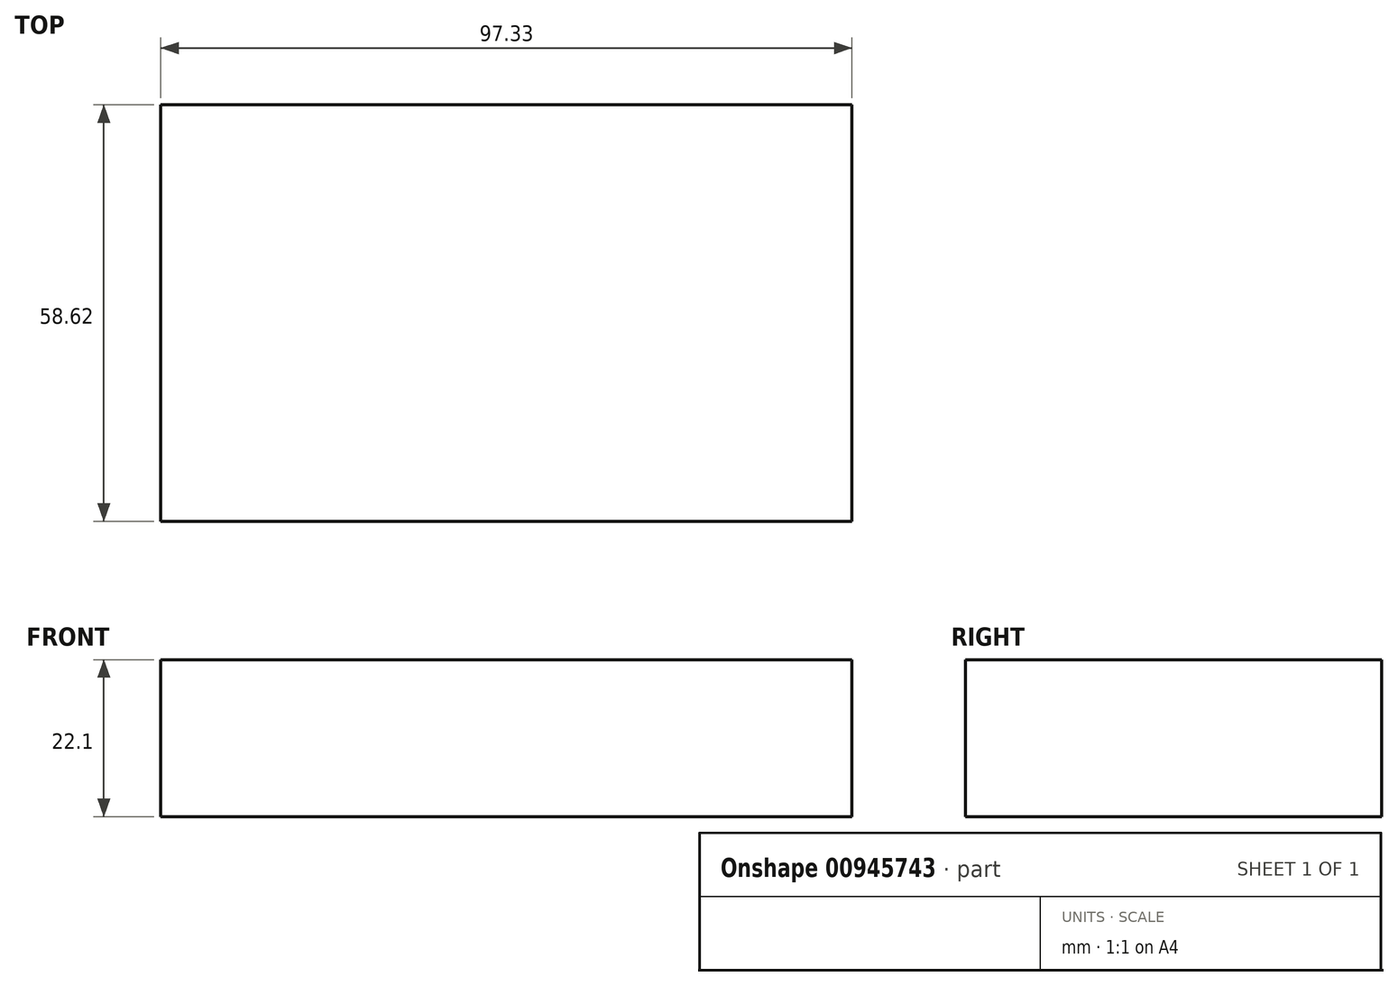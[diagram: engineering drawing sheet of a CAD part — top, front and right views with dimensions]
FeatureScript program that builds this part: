
annotation { "Feature Type Name" : "Feature", "Feature Type Description" : "" }
export const myFeature = defineFeature(function(context is Context, id is Id, definition is map)
    precondition{}
    {
        {
            var Q0;
            Q0=qCreatedBy(makeId("Top.planeOp"),FACE);
            var sketch = newSketch(context, id + "F0", { "sketchPlane" : qUnion([Q0])});
            skLineSegment(sketch, "E0.bottom", {"start": v(-48.02, 28.11) * mm, "end": v(49.31, 28.11) * mm});
            skLineSegment(sketch, "E0.top", {"start": v(-48.02, -30.51) * mm, "end": v(49.31, -30.51) * mm});
            skLineSegment(sketch, "E0.left", {"start": v(-48.02, 28.11) * mm, "end": v(-48.02, -30.51) * mm});
            skLineSegment(sketch, "E0.right", {"start": v(49.31, 28.11) * mm, "end": v(49.31, -30.51) * mm});
            skSolve(sketch);
        }
        {
            var Q0;
            Q0=makeQuery(id+"F0.imprint","IMPRINT",FACE,{"disambiguationData":[TD([[makeQuery(id+"F0.imprint","IMPRINT",EDGE,{"derivedFrom":sQuery(id+"F0.wireOp",EDGE,"E0.bottom")}),-1.0]])]});
            extrude(context, id + "F1", {"entities" : qUnion([Q0]), "depth" : 22.1 * mm, "offsetDistance" : 25.4 * mm});
        }
    });
